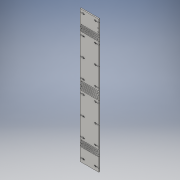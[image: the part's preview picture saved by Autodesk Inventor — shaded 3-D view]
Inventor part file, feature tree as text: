
AUTODESK INVENTOR PART (.ipt)
format: ipt  version: 2016 (Build 200138000, 138)  size: 486,912 bytes
history: native  units: in
note: dims shown in document units (in); Inventor stores cm internally (conversion verified against a paired STEP export)
features: extrude x2, sketch x2
ambient origin geometry x8: Origin, YZ Plane, XZ Plane, XY Plane, X Axis, Y Axis, Z Axis, Center Point
bodies: Solid1 (feature_tree)
feature tree (4):
  extrude  "Extrusion1"  Depth=0.1in
  extrude  "Extrusion2"  Depth=2.7414in
  sketch  "Sketch1"  dims[d34=0.427in d66=0.1in]
  sketch  "Sketch2"  dims[d94=2.7414in d95=2.7414in d109=0.305in d125=2.741in d127=0.6074in d128=0.6074in d130=0.6074in d162=0.942in d166=2.0in d167=2.0in d179=20.1074in d180=0.18in d181=0.0in d184=1.5in d188=1.5in d190=2.0in d191=0.9422in d192=2.84in d193=2.84in d194=2.84in d195=1.5in d197=0.1178in d198=0.1178in d199=0.1178in d200=2.2356in d201=1.5in d206=0.192in d207=2.84in d211=2.84in d212=2.84in d213=2.84in d214=2.84in d216=2.84in d217=2.84in d218=2.84in d219=2.84in d220=2.84in d221=2.84in d222=2.84in d223=0.427in d224=0.192in d228=2.84in d233=0.1in d234=0.1in d235=0.192in d236=0.1in d237=0.427in d238=0.192in d239=0.1in d240=0.427in d241=0.1923in d242=0.1004in d243=0.427in d244=0.1923in d245=0.1004in d246=0.427in d247=0.1004in d248=0.1923in d251=0.1004in d252=0.1923in d253=0.1923in d254=0.1004in d255=0.1923in d256=0.1004in d257=0.427in d258=0.1923in d259=0.1004in d260=0.427in d261=2.84in d262=0.1004in d263=0.1923in d264=0.1923in d265=0.427in d266=0.1in d267=0.192in d268=0.427in d269=0.192in d270=0.1in d271=0.427in d272=0.1in d273=0.192in d274=0.192in d275=0.1in d276=0.427in d277=0.192in d278=0.1in d279=0.427in d280=2.84in d281=2.84in d282=2.84in d283=2.84in d284=2.741in d285=2.741in d286=0.428in d287=0.062in d288=90.0deg d289=0.1in d290=0.192in d291=0.1in d292=0.062in d293=1.483in d294=0.252in d295=0.252in d296=0.12in d297=0.12in d298=0.1in d299=0.1in d300=1.0in d301=0.0in]
